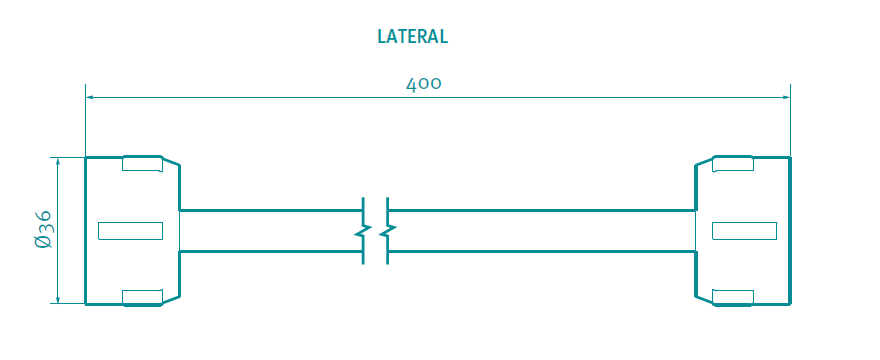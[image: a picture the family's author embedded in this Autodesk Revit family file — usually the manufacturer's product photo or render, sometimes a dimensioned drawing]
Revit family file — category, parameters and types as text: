
# Revit family: ACOPLE_PLASTICO_380140001
name_source: partatom
category: Pipe Accessories
units: mm (PartAtom-declared; Revit-internal decimal feet)

## family parameters
Always vertical = Yes
Cut with Voids When Loaded = No
OmniClass Number = 23.27.43.00
OmniClass Title = Pipe Fittings
Part Type = Normal
Round Connector Dimension = Use Diameter
Shared = No
Work Plane-Based = No

## types (1)
- ACOPLE_PLASTICO_380140001
    Depth = 150 mm
    Description = Adquiere ahora el conector plástico de alta flexibilidad para lavamanos o lavaplatos, cuenta con acabados en blanco mate. Está fabricado en plástico flexible y hecho con los más altos estándares de calidad.
    Diameter = 13 mm
    Gross Weight approx = 14 gr. (0,0309 lb.)
    Height = 250 mm  [stored 0.82021 ft]
    Intermittent impulse pressure (Life Cycle) = 100.000 Ciclos
    Material = Corona_Plastico_Blanco
    Maximum working pressure (gauge) = 125 Psi
    Minimum pressure = Presión mínima 20 Psi
    Net Weight approx = 10gr. (0.0220  lb.)
    Radius = 100 mm  [stored 0.328084 ft]
    URL = https://corona.co
    Warranty = 5 years
    Work Temperature = 4ºC - 71ºC (39,2ºF - 160ºF).

note: [stored X ft] marks values corroborated as IEEE doubles in the binary element streams (Revit-internal decimal feet)

## geometry (parser evidence)
native form markers: Sweep x7
no freeform markers — native parametric forms only
